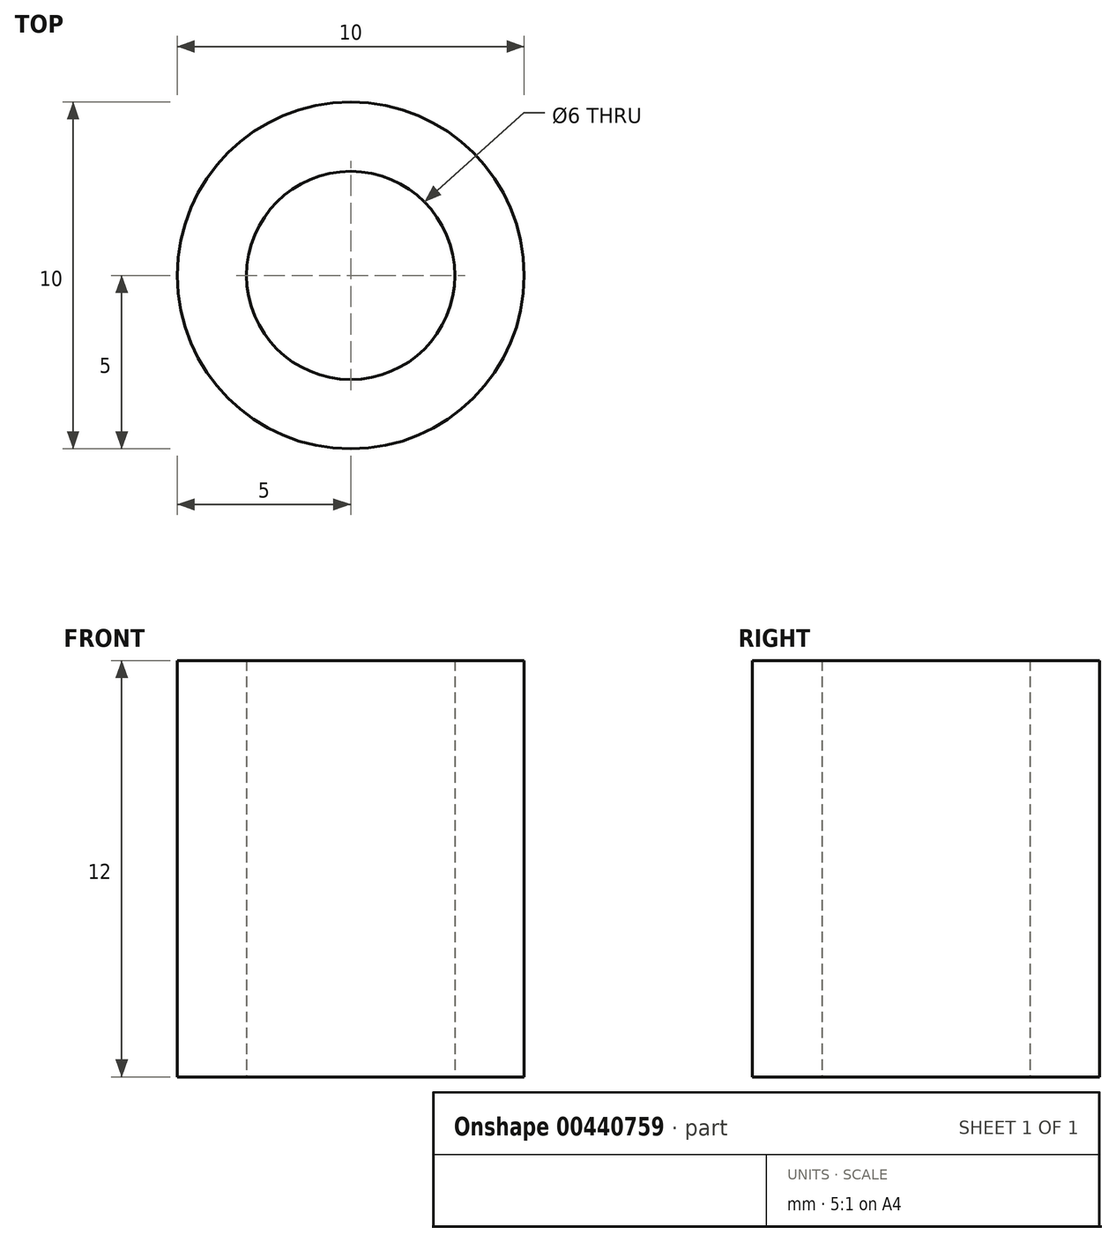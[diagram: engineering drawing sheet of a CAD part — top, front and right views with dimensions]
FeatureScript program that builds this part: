
annotation { "Feature Type Name" : "Feature", "Feature Type Description" : "" }
export const myFeature = defineFeature(function(context is Context, id is Id, definition is map)
    precondition{}
    {
        {
            var Q0;
            Q0=qCreatedBy(makeId("Top.planeOp"),FACE);
            var sketch = newSketch(context, id + "F0", { "sketchPlane" : qUnion([Q0])});
            skCircle(sketch, "E0", {"center": v(0, 0) * mm, "radius": 5 * mm});
            skCircle(sketch, "E1", {"center": v(0, 0) * mm, "radius": 3 * mm});
            skSolve(sketch);
        }
        {
            var Q0;
            Q0=makeQuery(id+"F0.imprint","IMPRINT",FACE,{"disambiguationData":[TD([[makeQuery(id+"F0.imprint","IMPRINT",EDGE,{"derivedFrom":sQuery(id+"F0.wireOp",EDGE,"E0")}),1.0]])]});
            extrude(context, id + "F1", {"entities" : qUnion([Q0]), "depth" : 12 * mm});
        }
    });
